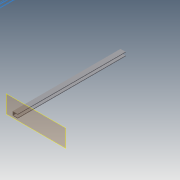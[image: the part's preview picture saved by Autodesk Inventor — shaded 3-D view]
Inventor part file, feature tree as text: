
AUTODESK INVENTOR PART (.ipt)
format: ipt  version: 2014 SP1 (Build 180222100, 222)  size: 76,800 bytes
history: native  units: in
note: dims shown in document units (in); Inventor stores cm internally (conversion verified against a paired STEP export)
features: plane x1, extrude x1, sketch x1
ambient origin geometry x8: Origin, YZ Plane, XZ Plane, XY Plane, X Axis, Y Axis, Z Axis, Center Point
bodies: Solid1 (feature_tree)
feature tree (3):
  plane  "Work Plane1"
  extrude  "Extrusion1"  Depth=0.5118in
  sketch  "Sketch1"  dims[d0=0.3937in d1=0.5118in d2=0.063in d3=0.063in d4=0.063in d5=11.2726in d6=0.0in]
